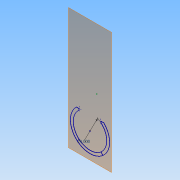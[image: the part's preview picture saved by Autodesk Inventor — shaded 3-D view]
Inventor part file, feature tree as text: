
AUTODESK INVENTOR PART (.ipt)
format: ipt  version: 2013 (Build 170138000, 138)  size: 74,240 bytes
history: native  units: in
note: dims shown in document units (in); Inventor stores cm internally (conversion verified against a paired STEP export)
features: plane x1, sketch x1, reference x1
ambient origin geometry x8: Origin, YZ Plane, XZ Plane, XY Plane, X Axis, Y Axis, Z Axis, Center Point
feature tree (3):
  plane  "Work Plane1"
  sketch  "Sketch1"  dims[d0=29.0in]
  reference  "Reference1"
